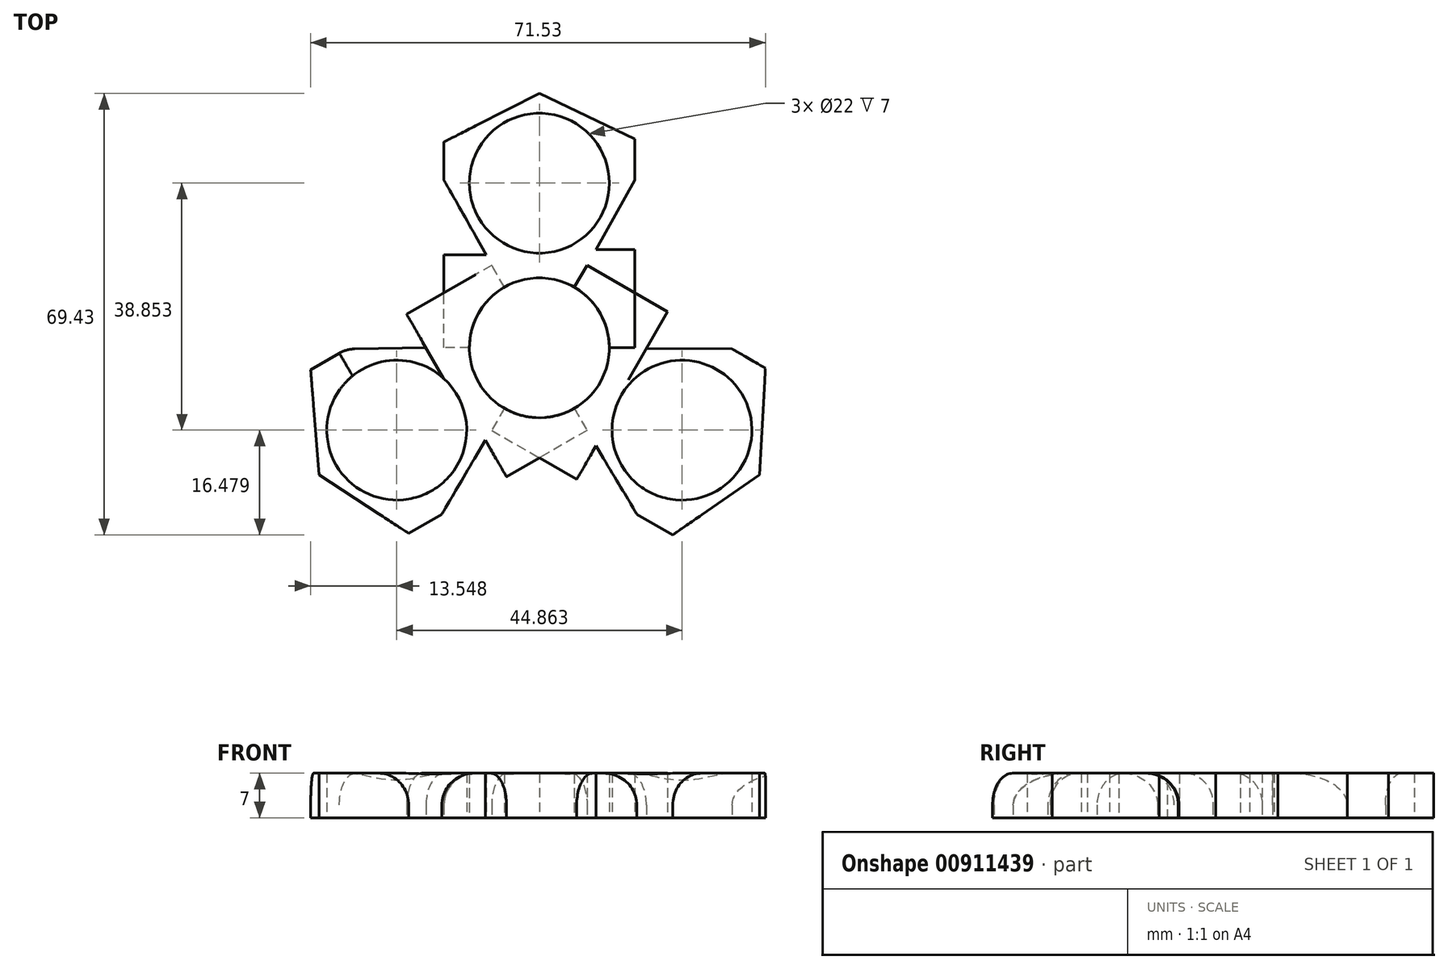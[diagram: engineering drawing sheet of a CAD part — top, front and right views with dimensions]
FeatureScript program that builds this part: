
annotation { "Feature Type Name" : "Feature", "Feature Type Description" : "" }
export const myFeature = defineFeature(function(context is Context, id is Id, definition is map)
    precondition{}
    {
        {
            var Q0;
            Q0=qCreatedBy(makeId("Top.planeOp"),FACE);
            var sketch = newSketch(context, id + "F0", { "sketchPlane" : qUnion([Q0])});
            skCircle(sketch, "E0", {"center": v(0, 0) * mm, "radius": 11 * mm});
            skLineSegment(sketch, "E1.bottom", {"start": v(0, 0) * mm, "end": v(15, 0) * mm});
            skLineSegment(sketch, "E1.top", {"start": v(0, 40) * mm, "end": v(15, 40) * mm});
            skLineSegment(sketch, "E1.left", {"start": v(0, 0) * mm, "end": v(0, 40) * mm});
            skLineSegment(sketch, "E1.right", {"start": v(15, 0) * mm, "end": v(15, 40) * mm});
            skLineSegment(sketch, "E2.bottom", {"start": v(0, 0) * mm, "end": v(-15, 0) * mm});
            skLineSegment(sketch, "E2.top", {"start": v(0, 40) * mm, "end": v(-15, 40) * mm});
            skLineSegment(sketch, "E2.right", {"start": v(-15, 0) * mm, "end": v(-15, 40) * mm});
            skLineSegment(sketch, "E3", {"start": v(0, 40) * mm, "end": v(0, 25.9) * mm});
            skCircle(sketch, "E4", {"center": v(0, 25.9) * mm, "radius": 11 * mm});
            skLineSegment(sketch, "E5", {"start": v(-15, 14.63) * mm, "end": v(-8.33, 14.63) * mm});
            skLineSegment(sketch, "E6", {"start": v(-8.33, 14.63) * mm, "end": v(-15, 26.37) * mm});
            skLineSegment(sketch, "E7", {"start": v(-15, 32.4) * mm, "end": v(0, 40) * mm});
            skLineSegment(sketch, "E8", {"start": v(0, 40) * mm, "end": v(15, 32.88) * mm});
            skLineSegment(sketch, "E9", {"start": v(15, 26.37) * mm, "end": v(8.91, 15.44) * mm});
            skLineSegment(sketch, "E10", {"start": v(8.91, 15.44) * mm, "end": v(15, 15.44) * mm});
            skSolve(sketch);
        }
        {
            var Q0;
            {var subQ10=sQuery(id+"F0.wireOp",EDGE,"E5");Q0=makeQuery(id+"F0.imprint","IMPRINT",FACE,{"disambiguationData":[TD([[makeQuery(id+"F0.imprint","IMPRINT",EDGE,{"derivedFrom":subQ10}),-1.0]])]});}
            var Q1;
            {var subQ8=sQuery(id+"F0.wireOp",EDGE,"E8");Q1=makeQuery(id+"F0.imprint","IMPRINT",FACE,{"disambiguationData":[TD([[makeQuery(id+"F0.imprint","IMPRINT",EDGE,{"derivedFrom":subQ8}),-1.0]])]});}
            extrude(context, id + "F1", {"entities" : qUnion([Q0, Q1]), "depth" : 7 * mm, "offsetDistance" : 25 * mm});
        }
        {
            var Q0;
            Q0=qCreatedBy(makeId("Front.planeOp"),FACE);
            var sketch = newSketch(context, id + "F2", { "sketchPlane" : qUnion([Q0])});
            skLineSegment(sketch, "E11", {"start": v(0, 0) * mm, "end": v(0, 51.62) * mm});
            skSolve(sketch);
        }
        {
            var Q0;
            Q0=makeQuery(id+"F1.opExtrude","SWEPT_BODY",BODY,{"disambiguationData":[OSD([sQuery(id+"F0.wireOp",EDGE,"E0"),sQuery(id+"F0.wireOp",EDGE,"E1.bottom"),sQuery(id+"F0.wireOp",EDGE,"E1.top"),sQuery(id+"F0.wireOp",EDGE,"E1.right"),sQuery(id+"F0.wireOp",EDGE,"E2.bottom"),sQuery(id+"F0.wireOp",EDGE,"E2.top"),sQuery(id+"F0.wireOp",EDGE,"E2.right"),sQuery(id+"F0.wireOp",EDGE,"E4")])]});
            var Q1;
            Q1=sQuery(id+"F2.wireOp",EDGE,"E11");
            transform(context, id + "F3", {"entities" : qUnion([Q0]), "transformType" : TransformType.ROTATION, "transformAxis" : qUnion([Q1]), "angle" : 120 * degree, "makeCopy" : true});
        }
        {
            var Q0;
            Q0=makeQuery(id+"F1.opExtrude","SWEPT_BODY",BODY,{"disambiguationData":[OSD([sQuery(id+"F0.wireOp",EDGE,"E0"),sQuery(id+"F0.wireOp",EDGE,"E1.bottom"),sQuery(id+"F0.wireOp",EDGE,"E1.top"),sQuery(id+"F0.wireOp",EDGE,"E1.right"),sQuery(id+"F0.wireOp",EDGE,"E2.bottom"),sQuery(id+"F0.wireOp",EDGE,"E2.top"),sQuery(id+"F0.wireOp",EDGE,"E2.right"),sQuery(id+"F0.wireOp",EDGE,"E4")])]});
            var Q1;
            Q1=sQuery(id+"F2.wireOp",EDGE,"E11");
            transform(context, id + "F4", {"entities" : qUnion([Q0]), "transformType" : TransformType.ROTATION, "transformAxis" : qUnion([Q1]), "angle" : 240 * degree, "makeCopy" : true});
        }
        {
            var Q0;
            Q0=makeQuery(id+"F1.opExtrude","CAP_EDGE",EDGE,{"disambiguationData":[OSD([sQuery(id+"F0.wireOp",EDGE,"E1.top"),sQuery(id+"F0.wireOp",EDGE,"E2.top")])],"isStart":false});
            var Q1;
            Q1=makeQuery(id+"F1.opExtrude","CAP_EDGE",EDGE,{"disambiguationData":[OSD([sQuery(id+"F0.wireOp",EDGE,"E2.right")])],"isStart":false});
            var Q2;
            Q2=makeQuery(id+"F3.opPattern","COPY",EDGE,{"derivedFrom":makeQuery(id+"F1.opExtrude","CAP_EDGE",EDGE,{"disambiguationData":[OSD([sQuery(id+"F0.wireOp",EDGE,"E1.right")])],"isStart":false}),"instanceName":"1"});
            var Q3;
            Q3=makeQuery(id+"F3.opPattern","COPY",EDGE,{"derivedFrom":makeQuery(id+"F1.opExtrude","CAP_EDGE",EDGE,{"disambiguationData":[OSD([sQuery(id+"F0.wireOp",EDGE,"E2.right")])],"isStart":false}),"instanceName":"1"});
            var Q4;
            Q4=makeQuery(id+"F4.opPattern","COPY",EDGE,{"derivedFrom":makeQuery(id+"F1.opExtrude","CAP_EDGE",EDGE,{"disambiguationData":[OSD([sQuery(id+"F0.wireOp",EDGE,"E1.right")])],"isStart":false}),"instanceName":"1"});
            var Q5;
            Q5=makeQuery(id+"F4.opPattern","COPY",EDGE,{"derivedFrom":makeQuery(id+"F1.opExtrude","CAP_EDGE",EDGE,{"disambiguationData":[OSD([sQuery(id+"F0.wireOp",EDGE,"E1.top"),sQuery(id+"F0.wireOp",EDGE,"E2.top")])],"isStart":false}),"instanceName":"1"});
            fillet(context, id + "F5", {"entities" : qUnion([Q0, Q1, Q2, Q3, Q4, Q5]), "radius" : 5 * mm, "tangentPropagation" : true, "allowEdgeOverflow" : false});
        }
        {
            var Q0;
            {var subQ0=sQuery(id+"F0.wireOp",EDGE,"E9");var subQ1=sQuery(id+"F0.wireOp",EDGE,"E1.right");Q0=makeQuery(id+"F5.opFillet","BLEND_EDGE",EDGE,{"blendedFrom":[makeQuery(id+"F3.opPattern","COPY",EDGE,{"derivedFrom":makeQuery(id+"F1.opExtrude","CAP_EDGE",EDGE,{"disambiguationData":[OSD([subQ1]),TDD([makeQuery(id+"F0.imprint","IMPRINT",EDGE,{"disambiguationData":[TD([[makeQuery(id+"F0.imprint","INTERSECT",VERTEX,{"derivedFrom":[subQ1,sQuery(id+"F0.wireOp",EDGE,"E8")]}),1.0]])],"derivedFrom":subQ1})])],"isStart":false}),"instanceName":"1"}),makeQuery(id+"F3.opPattern","COPY",FACE,{"derivedFrom":makeQuery(id+"F1.opExtrude","SWEPT_FACE",FACE,{"disambiguationData":[OSD([subQ0])]}),"instanceName":"1"})],"blendedInto":[makeQuery(id+"F3.opPattern","COPY",FACE,{"derivedFrom":makeQuery(id+"F1.opExtrude","SWEPT_FACE",FACE,{"disambiguationData":[OSD([subQ0])]}),"instanceName":"1"})]});}
            var Q1;
            Q1=makeQuery(id+"F4.opPattern","COPY",EDGE,{"derivedFrom":makeQuery(id+"F1.opExtrude","CAP_EDGE",EDGE,{"disambiguationData":[OSD([sQuery(id+"F0.wireOp",EDGE,"E6")])],"isStart":false}),"instanceName":"1"});
            fillet(context, id + "F6", {"entities" : qUnion([Q0, Q1]), "radius" : 5 * mm, "tangentPropagation" : true, "allowEdgeOverflow" : false});
        }
    });
